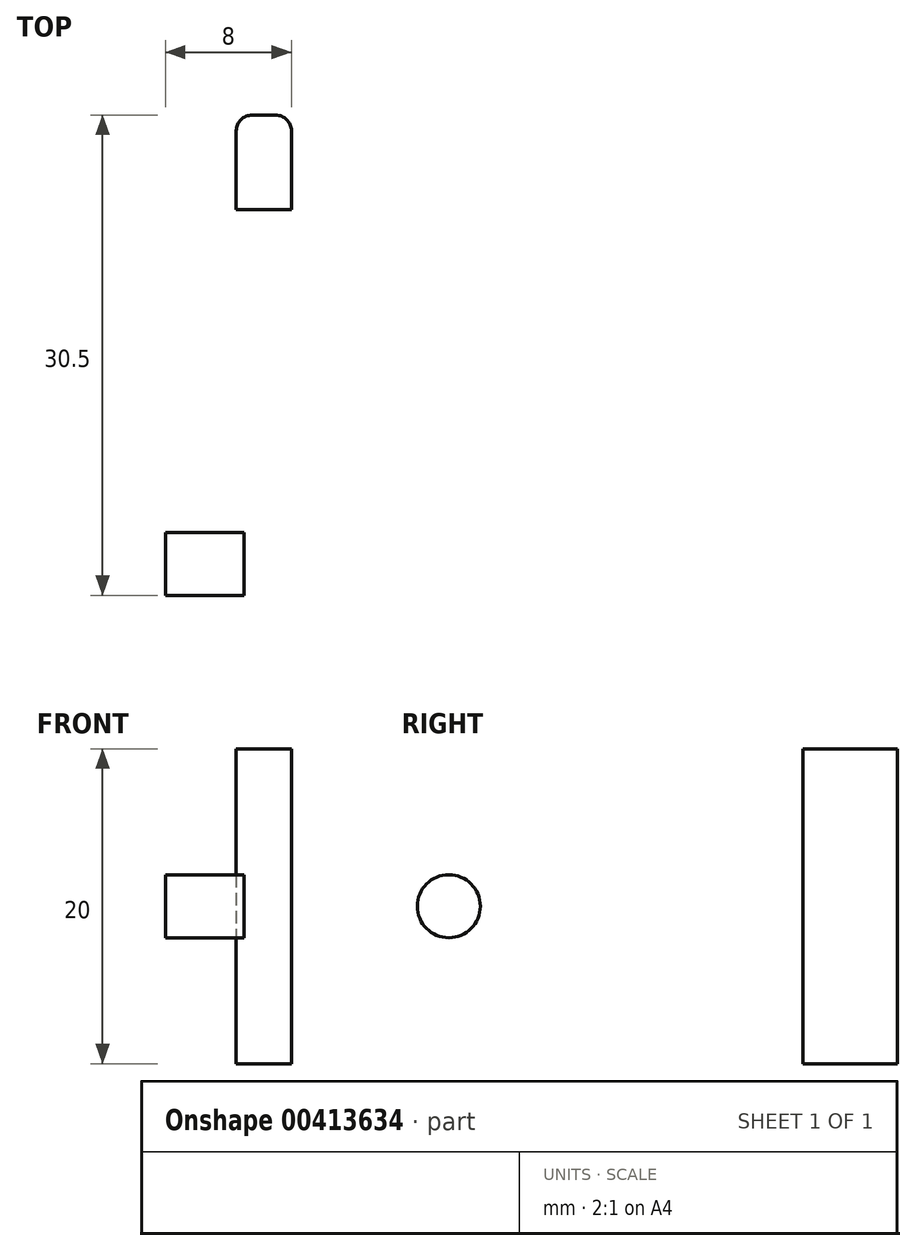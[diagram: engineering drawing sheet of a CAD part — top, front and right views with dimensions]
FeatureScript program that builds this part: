
annotation { "Feature Type Name" : "Feature", "Feature Type Description" : "" }
export const myFeature = defineFeature(function(context is Context, id is Id, definition is map)
    precondition{}
    {
        {
            var Q0;
            Q0=qCreatedBy(makeId("Top.planeOp"),FACE);
            var sketch = newSketch(context, id + "F0", { "sketchPlane" : qUnion([Q0])});
            skLineSegment(sketch, "E0", {"start": v(8, 36) * mm, "end": v(4.5, 36) * mm});
            skLineSegment(sketch, "E1", {"start": v(4.5, 36) * mm, "end": v(4.5, 30) * mm});
            skLineSegment(sketch, "E2", {"start": v(4.5, 30) * mm, "end": v(0, 30) * mm});
            skLineSegment(sketch, "E3", {"start": v(0, 30) * mm, "end": v(0, 0) * mm});
            skLineSegment(sketch, "E4", {"start": v(0, 0) * mm, "end": v(8, 0) * mm});
            skLineSegment(sketch, "E5", {"start": v(8, 0) * mm, "end": v(8, 36) * mm});
            skSolve(sketch);
        }
        {
            var Q0;
            Q0 = qSketchRegion(id + "F0", true);
            extrude(context, id + "F1", {"entities" : qUnion([Q0]), "depth" : 20 * mm});
        }
        {
            var Q0;
            Q0=makeQuery(id+"F1.opExtrude","SWEPT_FACE",FACE,{"disambiguationData":[OSD([sQuery(id+"F0.wireOp",EDGE,"E3")])]});
            var sketch = newSketch(context, id + "F2", { "sketchPlane" : qUnion([Q0])});
            skLineSegment(sketch, "E6", {"start": v(-30, 10) * mm, "end": v(0, 10) * mm, "construction": true});
            skLineSegment(sketch, "E7", {"start": v(-15, 0) * mm, "end": v(-15, 20) * mm, "construction": true});
            skCircle(sketch, "E8", {"center": v(-22.5, 10) * mm, "radius": 2 * mm});
            skCircle(sketch, "E9.MirrorC", {"center": v(-7.5, 10) * mm, "radius": 2 * mm});
            skSolve(sketch);
        }
        {
            var Q0;
            Q0=makeQuery(id+"F2.imprint","IMPRINT",FACE,{"disambiguationData":[TD([[makeQuery(id+"F2.imprint","IMPRINT",EDGE,{"derivedFrom":sQuery(id+"F2.wireOp",EDGE,"E9.MirrorC")}),-1.0]])]});
            var Q1;
            Q1=makeQuery(id+"F2.imprint","IMPRINT",FACE,{"disambiguationData":[TD([[makeQuery(id+"F2.imprint","IMPRINT",EDGE,{"derivedFrom":sQuery(id+"F2.wireOp",EDGE,"E8")}),1.0]])]});
            var Q2;
            Q2=sQuery(id+"F2.wireOp",EDGE,"E6");
            var Q3;
            Q3=sQuery(id+"F2.wireOp",EDGE,"E7");
            extrude(context, id + "F3", {"entities" : qUnion([Q0, Q1]), "operationType" : NewBodyOperationType.REMOVE, "surfaceEntities" : qUnion([Q2, Q3]), "endBound" : BoundingType.THROUGH_ALL, "oppositeDirection" : true, "depth" : 25 * mm});
        }
        {
            var Q0;
            Q0=makeQuery(id+"F1.opExtrude","SWEPT_EDGE",EDGE,{"disambiguationData":[OSD([sQuery(id+"F0.wireOp",EDGE,"E0"),sQuery(id+"F0.wireOp",EDGE,"E1")])]});
            var Q1;
            Q1=makeQuery(id+"F1.opExtrude","SWEPT_EDGE",EDGE,{"disambiguationData":[OSD([sQuery(id+"F0.wireOp",EDGE,"E0"),sQuery(id+"F0.wireOp",EDGE,"E5")])]});
            fillet(context, id + "F4", {"entities" : qUnion([Q0, Q1]), "radius" : 1 * mm, "tangentPropagation" : true, "allowEdgeOverflow" : false});
        }
        {
            var Q0;
            Q0=makeQuery(id+"F1.opExtrude","SWEPT_FACE",FACE,{"disambiguationData":[OSD([sQuery(id+"F0.wireOp",EDGE,"E5")])]});
            var sketch = newSketch(context, id + "F5", { "sketchPlane" : qUnion([Q0])});
            skCircle(sketch, "E10", {"center": v(22.5, 10) * mm, "radius": 4.25 * mm});
            skCircle(sketch, "E11", {"center": v(7.5, 10) * mm, "radius": 4.25 * mm});
            skSolve(sketch);
        }
        {
            var Q0;
            Q0 = qSketchRegion(id + "F5", true);
            extrude(context, id + "F6", {"entities" : qUnion([Q0]), "operationType" : NewBodyOperationType.REMOVE, "oppositeDirection" : true, "depth" : 3 * mm});
        }
    });
